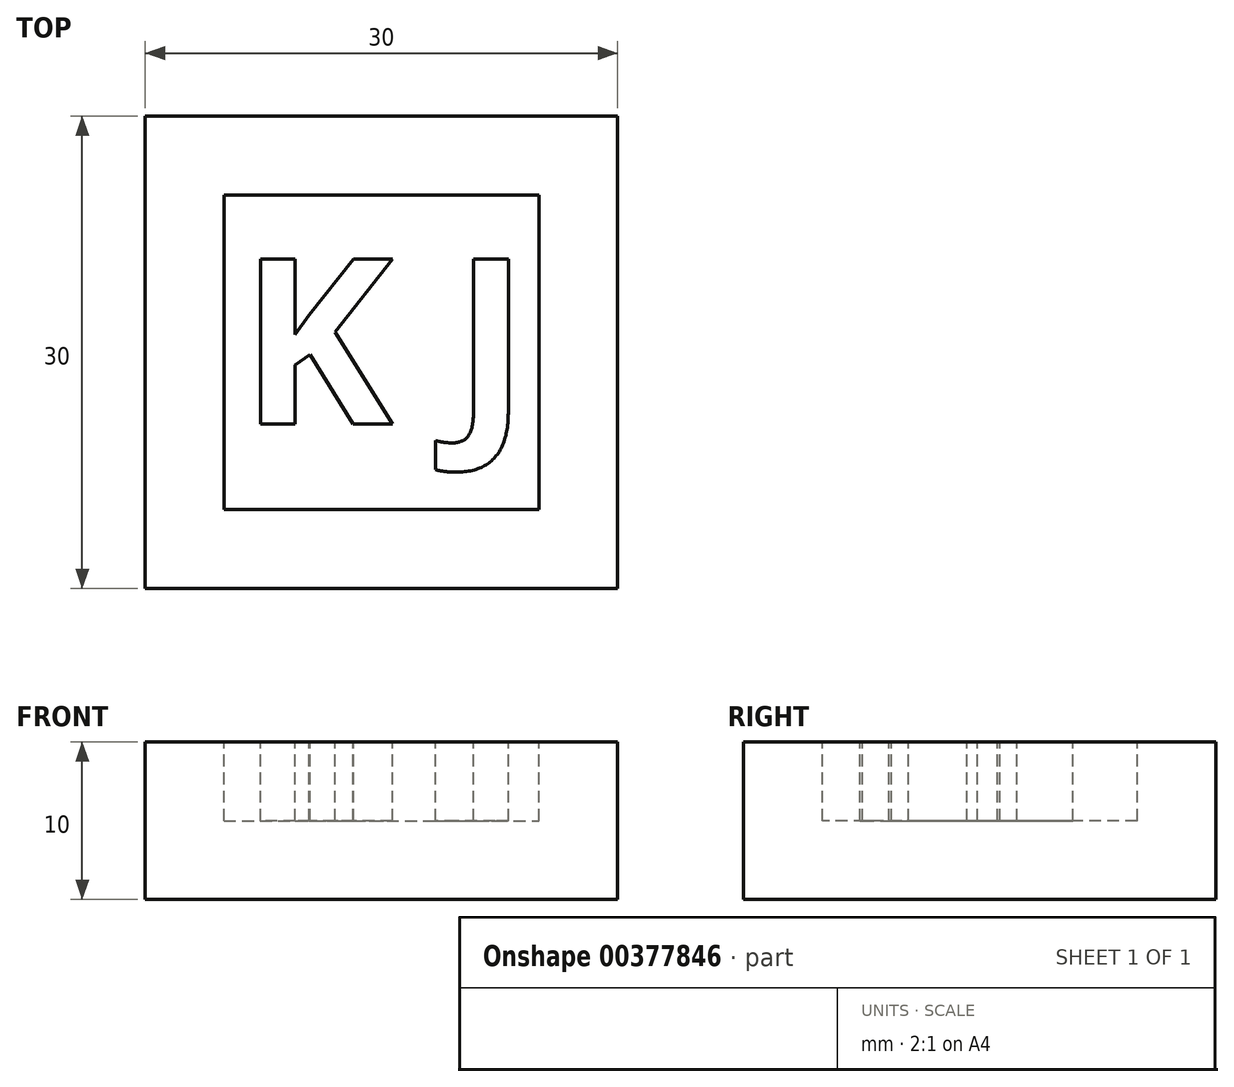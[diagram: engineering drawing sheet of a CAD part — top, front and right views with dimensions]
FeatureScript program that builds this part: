
annotation { "Feature Type Name" : "Feature", "Feature Type Description" : "" }
export const myFeature = defineFeature(function(context is Context, id is Id, definition is map)
    precondition{}
    {
        {
            var Q0;
            Q0=qCreatedBy(makeId("Top.planeOp"),FACE);
            var sketch = newSketch(context, id + "F0", { "sketchPlane" : qUnion([Q0])});
            skLineSegment(sketch, "E0", {"start": v(0, 21.61) * mm, "end": v(0, -23.43) * mm, "construction": true});
            skLineSegment(sketch, "E1.bottom", {"start": v(-15, 15) * mm, "end": v(15, 15) * mm});
            skLineSegment(sketch, "E1.top", {"start": v(-15, -15) * mm, "end": v(15, -15) * mm});
            skLineSegment(sketch, "E1.left", {"start": v(-15, 15) * mm, "end": v(-15, -15) * mm});
            skLineSegment(sketch, "E1.right", {"start": v(15, 15) * mm, "end": v(15, -15) * mm});
            skLineSegment(sketch, "E2", {"start": v(0, 0) * mm, "end": v(37.6, 0) * mm, "construction": true});
            skSolve(sketch);
        }
        {
            var Q0;
            Q0=makeQuery(id+"F0.imprint","IMPRINT",FACE,{"disambiguationData":[TD([[makeQuery(id+"F0.imprint","IMPRINT",EDGE,{"derivedFrom":sQuery(id+"F0.wireOp",EDGE,"E1.bottom")}),-1.0]])]});
            extrude(context, id + "F1", {"entities" : qUnion([Q0]), "depth" : 10 * mm});
        }
        {
            var Q0;
            Q0=makeQuery(id+"F1.opExtrude","CAP_FACE",FACE,{"disambiguationData":[OSD([sQuery(id+"F0.wireOp",EDGE,"E1.bottom"),sQuery(id+"F0.wireOp",EDGE,"E1.top"),sQuery(id+"F0.wireOp",EDGE,"E1.left"),sQuery(id+"F0.wireOp",EDGE,"E1.right")])],"isStart":false});
            var sketch = newSketch(context, id + "F2", { "sketchPlane" : qUnion([Q0])});
            skLineSegment(sketch, "E3.bottom", {"start": v(-10, 10) * mm, "end": v(10, 10) * mm});
            skLineSegment(sketch, "E3.top", {"start": v(-10, -10) * mm, "end": v(10, -10) * mm});
            skLineSegment(sketch, "E3.left", {"start": v(-10, 10) * mm, "end": v(-10, -10) * mm});
            skLineSegment(sketch, "E3.right", {"start": v(10, 10) * mm, "end": v(10, -10) * mm});
            skLineSegment(sketch, "E4.bottom", {"start": v(-15, 15) * mm, "end": v(15, 15) * mm});
            skLineSegment(sketch, "E4.top", {"start": v(-15, -15) * mm, "end": v(15, -15) * mm});
            skLineSegment(sketch, "E4.left", {"start": v(-15, 15) * mm, "end": v(-15, -15) * mm});
            skLineSegment(sketch, "E4.right", {"start": v(15, 15) * mm, "end": v(15, -15) * mm});
            skLineSegment(sketch, "E5.bottom", {"start": v(0, 25.22) * mm, "end": v(0, 25.22) * mm});
            skLineSegment(sketch, "E5.top", {"start": v(0, -31.2) * mm, "end": v(0, -31.2) * mm});
            skLineSegment(sketch, "E5.left", {"start": v(0, 25.22) * mm, "end": v(0, -31.2) * mm, "construction": true});
            skLineSegment(sketch, "E5.right", {"start": v(0, 25.22) * mm, "end": v(0, -31.2) * mm, "construction": true});
            skText(sketch, "E6", { "text": "K J", "fontName": "OpenSans-Bold.ttf"});
            const initialGuessF2  = {"E6": [-0.009, -0.00454, 1, 0, 0.01054]};
            skSetInitialGuess(sketch, initialGuessF2);
            skSolve(sketch);
        }
        {
            var Q0;
            Q0=makeQuery(id+"F2.imprint","IMPRINT",FACE,{"disambiguationData":[TD([[makeQuery(id+"F2.imprint","IMPRINT",EDGE,{"derivedFrom":sQuery(id+"F2.wireOp",EDGE,"E3.bottom")}),-1.0]])]});
            extrude(context, id + "F3", {"entities" : qUnion([Q0]), "operationType" : NewBodyOperationType.REMOVE, "oppositeDirection" : true, "depth" : 5 * mm});
        }
    });
